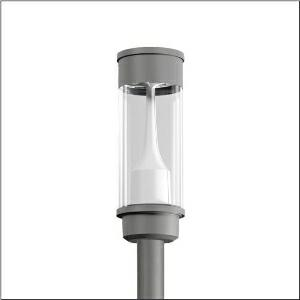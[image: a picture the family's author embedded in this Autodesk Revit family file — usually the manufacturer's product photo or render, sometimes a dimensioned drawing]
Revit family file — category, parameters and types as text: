
# Revit family: litepole_iq___p1_0a_5xa5415ff14h000022_df26
name_source: partatom
category: Lighting Fixtures
units: mm (PartAtom-declared; Revit-internal decimal feet)

## family parameters
Cut with Voids When Loaded = No
Host = Face
Light Source = No
Part Type = Normal
Room Calculation Point = No
Round Connector Dimension = Use Diameter
Shared = No

## types (1)
- --- (1 x LED, 1510 lm, 10.5 W, 3000K)
    Apparent Load = 11 VA
    CIE Flux Codes = 32 61 90 93 100
    Color Rendering = 70
    Color Temperature = 3000K
    Default Elevation = 1800 mm
    Description = Litepole iQ, mast luminaire, Module 540 iQ-SR, primary light control with 3 zone facetted reflector, of plastic, silver coated, highly specular, structured, primary optical cover: cover, of PMMA, transparent, light distribution: P1.0a, light emission: direct distribution, primary light characteristic: strongly asymmetric, installation type: post-top, LED, High Power LED, rated luminous flux: 1.510lm, luminous efficacy: 144lm/W, light colour: 730, colour temperature: 3000K, control gear: iQ Street-Remote, control: Street-Remote, Auto-Match, Temp-Guard, Lumen-Switch, Night-Set, Smart-Wire, Light-Fading, Desk-Remote (wireless, voltage-free reading and setting of iQ features in the workshop via application-optimized NFC function/RFID function), optimised constant luminous flux control (CLO 2.0), pre-setting: logarithmic dimming characteristic, mains connection: 230..240V, AC, 50/60Hz, connection cable pre-assembled, cable length: 5,5m, wiring characteristics: H07RN-F, start of lifetime: 11W, end of service life: 11W, reduction: 5W, luminaire housing, upper part, of glass-fibre reinforced polyester, coated, Siteco® metallic grey (DB 702S), diameter: 210mm, height: 590mm, spigot size: d x l = 76 x 70mm (post-top) | with reducer (optional accessory) 60 x 70mm, mounting height: 3..5m, post-top mast mounting element, of diecast aluminium, coated, Siteco® metallic grey (DB 702S), Module 540 iQ-SR, traffic white (RAL 9016), equipment: standard, protection rating (complete): IP65, insulation class (complete): insulation class II (safety insulation), certification: CE, ENEC, VDE, packaging unit: 1 piece

Light Distribution: P1.0a
    Height = 590 mm
    Lamp = 1 x LED
    Lamp Light Flux = 1510 lm
    Lamp Power = 10.5 W
    Lamp count = 1
    Length = 220 mm
    Luminous efficacy = 144 lm/W
    Manufacturer = Siteco
    ModVariant = No
    Model = 5XA5415FF14H000022
    Number of Poles = 1
    OnlyDefault = Yes
    Power Factor = 1
    Product Name = Litepole iQ | P1.0a
    Product group = mast luminaire | pylon top
    ProductGroupID = 6100
    Protection Class = Protection class II
    Protection Degree = IP 65
    RLX_Detail_Level = 1
    RLX_Emergency_Light_Flux = 0 lm
    RLX_Emergency_Type = 0
    RLX_Emergency_Type_DB = No
    RlxData = <blob elided: 26845 chars, md5=c38982ec>
    Socket = socket
    Standby Power = 0 W
    System Light Flux = 1510 lm
    System Power = 11 W
    Type Comments = factory setting: luminous flux: 100 % | dim-lin: 254 | 419 mA
    Type Image = l_1006025.jpg
    URL = http://relux.com
    VarID = @adj_180131
    Voltage = 0 V
    Weight = 0.00 kg
    Width = 0 mm  [stored 0 ft]

note: [stored X ft] marks values corroborated as IEEE doubles in the binary element streams (Revit-internal decimal feet)

## geometry (parser evidence)
native form markers: Blend x4, Sweep x16
no freeform markers — native parametric forms only
